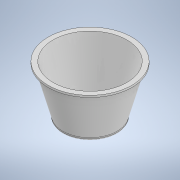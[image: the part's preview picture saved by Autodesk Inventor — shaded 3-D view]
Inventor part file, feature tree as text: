
AUTODESK INVENTOR PART (.ipt)
format: ipt  version: 2020 (Build 240168000, 168)  size: 291,328 bytes
history: native  units: mm
features: sketch x2, revolve x1, fillet x1
ambient origin geometry x8: Origin, YZ Plane, XZ Plane, XY Plane, X Axis, Y Axis, Z Axis, Center Point
bodies: Solid1 (feature_tree)
feature tree (4):
  sketch  "Sketch1"  dims[d0=25.0mm d1=50.0mm d2=105.0deg]
  sketch  "Sketch2"  dims[d3=5.0mm d4=2.0mm d5=3.0mm d6=105.0deg d7=3.0mm d8=90.0deg d9=2.0mm d10=0.5mm d11=0.872665mm]
  revolve  "Revolution1"  [1 undecoded]
  fillet  "Fillet1"  [1 undecoded]
note: 2 required parameter values undecoded (feature->parameter linkage not recoverable at this tier; creation-order binding heuristic only, values carry confidence <= 0.55)